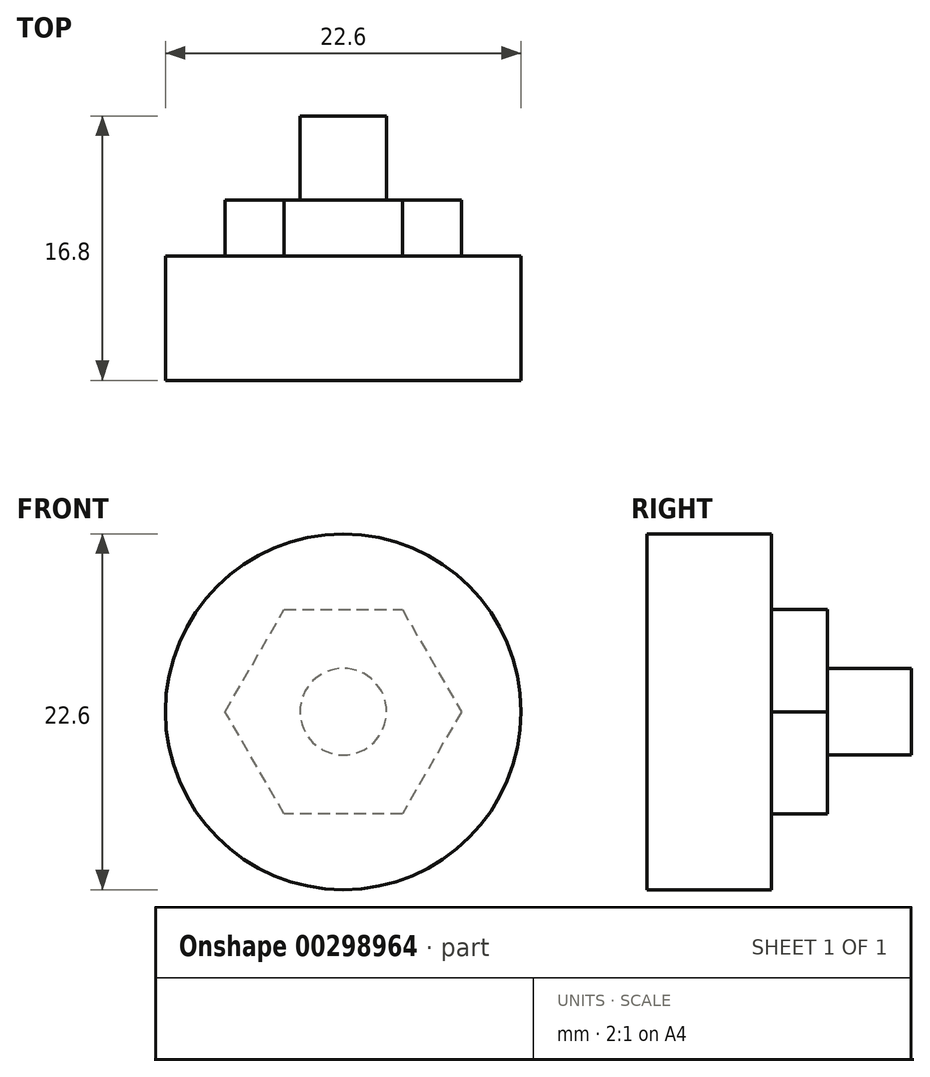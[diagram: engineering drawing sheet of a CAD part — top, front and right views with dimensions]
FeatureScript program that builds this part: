
annotation { "Feature Type Name" : "Feature", "Feature Type Description" : "" }
export const myFeature = defineFeature(function(context is Context, id is Id, definition is map)
    precondition{}
    {
        {
            var Q0;
            Q0=qCreatedBy(makeId("Front.planeOp"),FACE);
            var sketch = newSketch(context, id + "F0", { "sketchPlane" : qUnion([Q0])});
            skCircle(sketch, "E0", {"center": v(0, 0) * mm, "radius": 11.3 * mm});
            skSolve(sketch);
        }
        {
            var Q0;
            Q0 = qSketchRegion(id + "F0", true);
            var Q1;
            Q1=makeQuery(id+"F0.imprint","IMPRINT",FACE,{"disambiguationData":[TD([[makeQuery(id+"F0.imprint","IMPRINT",EDGE,{"derivedFrom":sQuery(id+"F0.wireOp",EDGE,"E0")}),1.0]])]});
            extrude(context, id + "F1", {"entities" : qUnion([Q0, Q1]), "depth" : 7.9 * mm});
        }
        {
            var Q0;
            Q0=qCreatedBy(makeId("Front.planeOp"),FACE);
            var sketch = newSketch(context, id + "F2", { "sketchPlane" : qUnion([Q0])});
            skCircle(sketch, "E1.cCircle", {"center": v(0, 0) * mm, "radius": 7.5 * mm, "construction": true});
            skLineSegment(sketch, "E1.0", {"start": v(-7.5, 0) * mm, "end": v(-3.75, 6.5) * mm});
            skLineSegment(sketch, "E1.1", {"start": v(-3.75, 6.5) * mm, "end": v(3.75, 6.5) * mm});
            skLineSegment(sketch, "E1.2", {"start": v(3.75, 6.5) * mm, "end": v(7.5, 0) * mm});
            skLineSegment(sketch, "E1.3", {"start": v(7.5, 0) * mm, "end": v(3.75, -6.5) * mm});
            skLineSegment(sketch, "E1.4", {"start": v(3.75, -6.5) * mm, "end": v(-3.75, -6.5) * mm});
            skLineSegment(sketch, "E1.5", {"start": v(-3.75, -6.5) * mm, "end": v(-7.5, 0) * mm});
            skSolve(sketch);
        }
        {
            var Q0;
            Q0 = qSketchRegion(id + "F2", true);
            extrude(context, id + "F3", {"entities" : qUnion([Q0]), "operationType" : NewBodyOperationType.ADD, "oppositeDirection" : true, "depth" : 3.55 * mm});
        }
        {
            var Q0;
            Q0=makeQuery(id+"F3.opExtrude","CAP_FACE",FACE,{"disambiguationData":[OSD([sQuery(id+"F2.wireOp",EDGE,"E1.0"),sQuery(id+"F2.wireOp",EDGE,"E1.1"),sQuery(id+"F2.wireOp",EDGE,"E1.2"),sQuery(id+"F2.wireOp",EDGE,"E1.3"),sQuery(id+"F2.wireOp",EDGE,"E1.4"),sQuery(id+"F2.wireOp",EDGE,"E1.5")])],"isStart":false});
            var sketch = newSketch(context, id + "F4", { "sketchPlane" : qUnion([Q0])});
            skCircle(sketch, "E2", {"center": v(0, 0) * mm, "radius": 2.75 * mm});
            skSolve(sketch);
        }
        {
            var Q0;
            Q0 = qSketchRegion(id + "F4", true);
            extrude(context, id + "F5", {"entities" : qUnion([Q0]), "operationType" : NewBodyOperationType.ADD, "depth" : 5.35 * mm});
        }
    });
